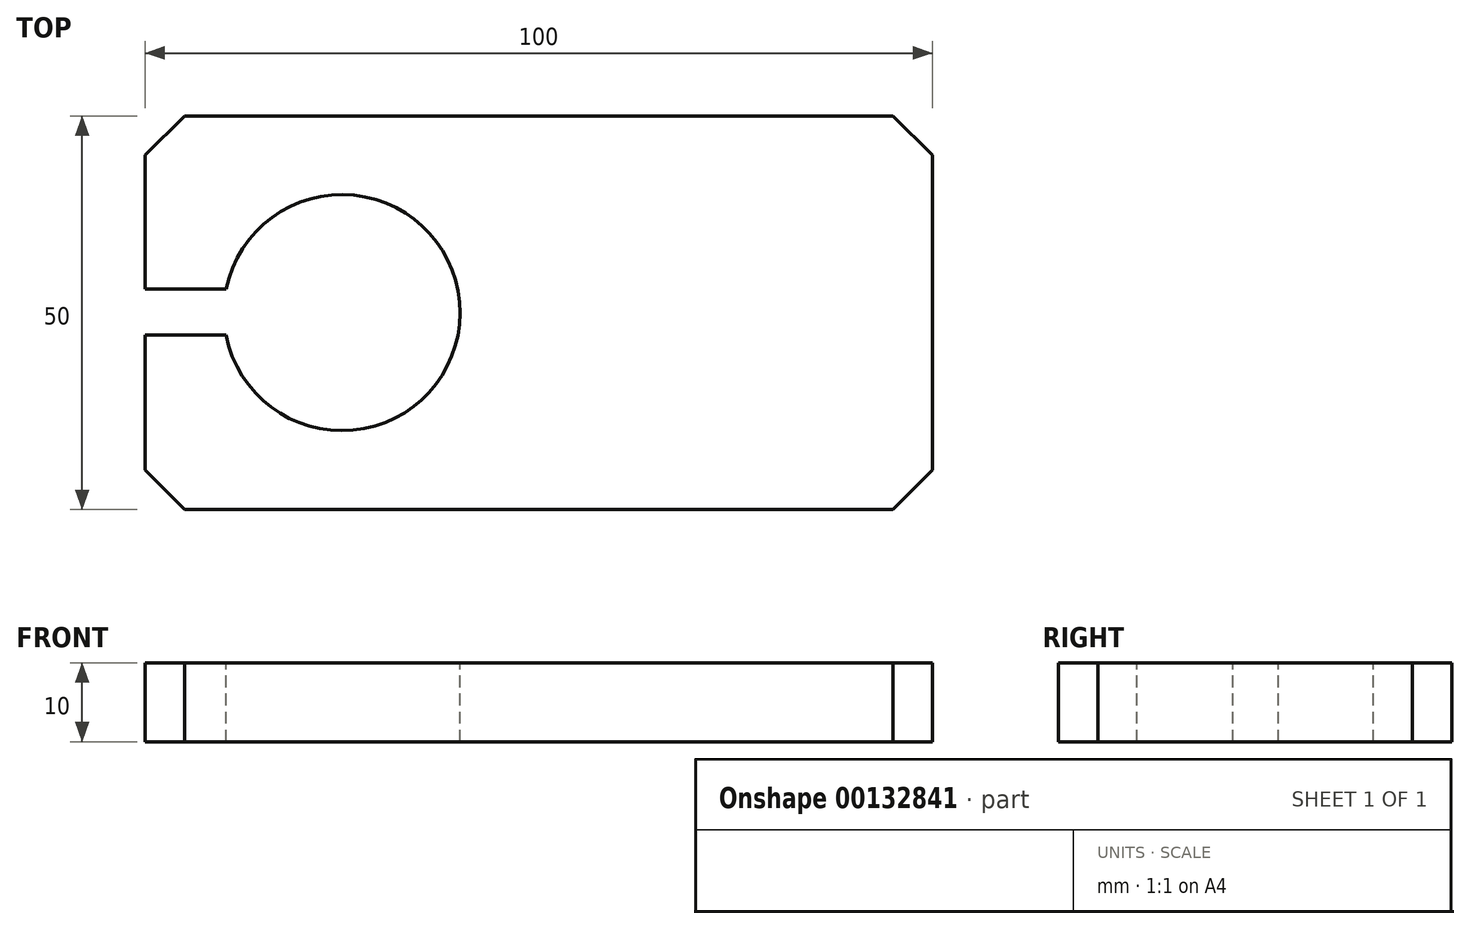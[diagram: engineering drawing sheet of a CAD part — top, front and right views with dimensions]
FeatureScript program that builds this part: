
annotation { "Feature Type Name" : "Feature", "Feature Type Description" : "" }
export const myFeature = defineFeature(function(context is Context, id is Id, definition is map)
    precondition{}
    {
        {
            var Q0;
            Q0=qCreatedBy(makeId("Top.planeOp"),FACE);
            var sketch = newSketch(context, id + "F0", { "sketchPlane" : qUnion([Q0])});
            skLineSegment(sketch, "E0.bottom", {"start": v(-50, -25) * mm, "end": v(50, -25) * mm});
            skLineSegment(sketch, "E0.top", {"start": v(-50, 25) * mm, "end": v(50, 25) * mm});
            skLineSegment(sketch, "E0.left", {"start": v(-50, -25) * mm, "end": v(-50, 25) * mm});
            skLineSegment(sketch, "E0.right", {"start": v(50, -25) * mm, "end": v(50, 25) * mm});
            skPoint(sketch, "E0.middle", {"position": v(0, 0) * mm});
            skSolve(sketch);
        }
        {
            var Q0;
            Q0=makeQuery(id+"F0.imprint","IMPRINT",FACE,{"disambiguationData":[TD([[makeQuery(id+"F0.imprint","IMPRINT",EDGE,{"derivedFrom":sQuery(id+"F0.wireOp",EDGE,"E0.bottom")}),1.0]])]});
            extrude(context, id + "F1", {"entities" : qUnion([Q0]), "depth" : 10 * mm});
        }
        {
            var Q0;
            Q0=makeQuery(id+"F1.opExtrude","CAP_FACE",FACE,{"disambiguationData":[OSD([sQuery(id+"F0.wireOp",EDGE,"E0.bottom"),sQuery(id+"F0.wireOp",EDGE,"E0.top"),sQuery(id+"F0.wireOp",EDGE,"E0.left"),sQuery(id+"F0.wireOp",EDGE,"E0.right")])],"isStart":false});
            var sketch = newSketch(context, id + "F2", { "sketchPlane" : qUnion([Q0])});
            skArc(sketch, "E1", {"start": v(-39.73, -2.85) * mm, "mid": v(-10, -0.06) * mm, "end": v(-39.7, 2.98) * mm});
            skLineSegment(sketch, "E2", {"start": v(-25, 0) * mm, "end": v(-50, 0) * mm, "construction": true});
            skLineSegment(sketch, "E3", {"start": v(-50, 2.98) * mm, "end": v(-39.7, 2.98) * mm});
            skLineSegment(sketch, "E4", {"start": v(-39.73, -2.85) * mm, "end": v(-50, -2.85) * mm});
            skLineSegment(sketch, "E5", {"start": v(-50, -2.85) * mm, "end": v(-50, 2.98) * mm});
            skSolve(sketch);
        }
        {
            var Q0;
            Q0 = qSketchRegion(id + "F2", true);
            extrude(context, id + "F3", {"entities" : qUnion([Q0]), "operationType" : NewBodyOperationType.REMOVE, "oppositeDirection" : true, "depth" : 25 * mm});
        }
        {
            var Q0;
            Q0=makeQuery(id+"F1.opExtrude","SWEPT_EDGE",EDGE,{"disambiguationData":[OSD([sQuery(id+"F0.wireOp",EDGE,"E0.top"),sQuery(id+"F0.wireOp",EDGE,"E0.right")])]});
            var Q1;
            Q1=makeQuery(id+"F1.opExtrude","SWEPT_EDGE",EDGE,{"disambiguationData":[OSD([sQuery(id+"F0.wireOp",EDGE,"E0.bottom"),sQuery(id+"F0.wireOp",EDGE,"E0.right")])]});
            var Q2;
            Q2=makeQuery(id+"F1.opExtrude","SWEPT_EDGE",EDGE,{"disambiguationData":[OSD([sQuery(id+"F0.wireOp",EDGE,"E0.top"),sQuery(id+"F0.wireOp",EDGE,"E0.left")])]});
            var Q3;
            Q3=makeQuery(id+"F1.opExtrude","SWEPT_EDGE",EDGE,{"disambiguationData":[OSD([sQuery(id+"F0.wireOp",EDGE,"E0.bottom"),sQuery(id+"F0.wireOp",EDGE,"E0.left")])]});
            chamfer(context, id + "F4", {"entities" : qUnion([Q0, Q1, Q2, Q3]), "width" : 5 * mm, "tangentPropagation" : true});
        }
    });
